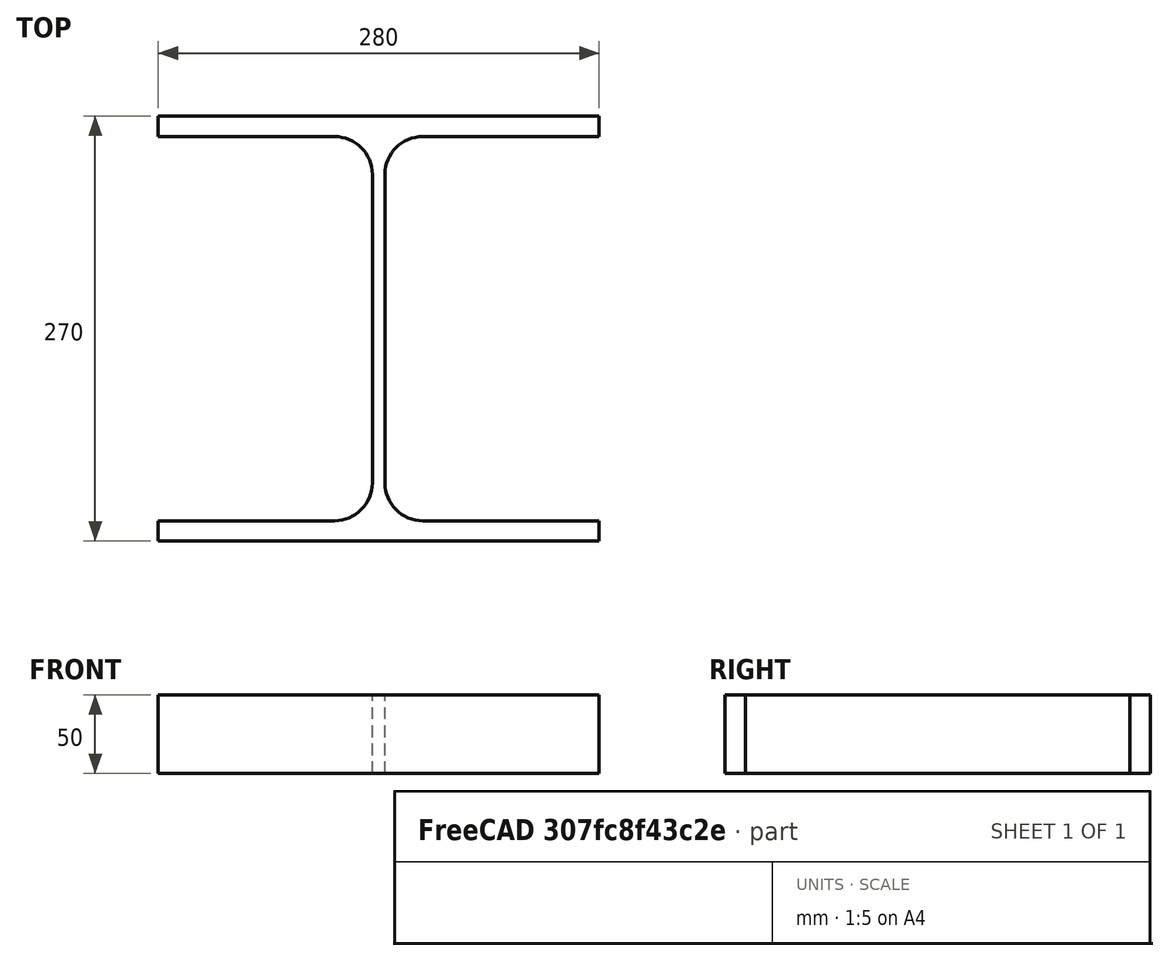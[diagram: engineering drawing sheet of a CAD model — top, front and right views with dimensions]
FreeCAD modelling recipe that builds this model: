
FCSTD DOCUMENT  (FreeCAD 0.15R4671 (Git))
Label: HE-A-Profile 280 DIN1025-3 S235JR
License: All rights reserved
LicenseURL: http://en.wikipedia.org/wiki/All_rights_reserved
objects: Sketcher::SketchObject×1, Part::Extrusion×1
note: 2 computed .brp shape members not serialized (recipe doc carries the construction recipe); baked Part::Feature solids carry a one-line shape summary decoded from their .brp

FEATURE [Sketcher::SketchObject] Sketch
  sketch-geometry (16):
    g0: LineSegment StartX=4 StartY=-98 StartZ=0 EndX=4 EndY=98 EndZ=0
    g1: LineSegment StartX=28 StartY=122 StartZ=0 EndX=140 EndY=122 EndZ=0
    g2: LineSegment StartX=140 StartY=122 StartZ=0 EndX=140 EndY=135 EndZ=0
    g3: LineSegment StartX=140 StartY=135 StartZ=0 EndX=-140 EndY=135 EndZ=0
    g4: LineSegment StartX=-140 StartY=135 StartZ=0 EndX=-140 EndY=122 EndZ=0
    g5: LineSegment StartX=-140 StartY=122 StartZ=0 EndX=-28 EndY=122 EndZ=0
    g6: LineSegment StartX=-4 StartY=98 StartZ=0 EndX=-4 EndY=-98 EndZ=0
    g7: LineSegment StartX=-28 StartY=-122 StartZ=0 EndX=-140 EndY=-122 EndZ=0
    g8: LineSegment StartX=-140 StartY=-122 StartZ=0 EndX=-140 EndY=-135 EndZ=0
    g9: LineSegment StartX=-140 StartY=-135 StartZ=0 EndX=140 EndY=-135 EndZ=0
    g10: LineSegment StartX=140 StartY=-135 StartZ=0 EndX=140 EndY=-122 EndZ=0
    g11: LineSegment StartX=140 StartY=-122 StartZ=0 EndX=28 EndY=-122 EndZ=0
    g12: ArcOfCircle CenterX=28 CenterY=98 CenterZ=0 NormalX=0 NormalY=0 NormalZ=1 Radius=24 StartAngle=1.5708 EndAngle=3.14159
    g13: ArcOfCircle CenterX=28 CenterY=-98 CenterZ=0 NormalX=0 NormalY=0 NormalZ=1 Radius=24 StartAngle=3.14159 EndAngle=4.71239
    g14: ArcOfCircle CenterX=-28 CenterY=98 CenterZ=0 NormalX=0 NormalY=0 NormalZ=1 Radius=24 StartAngle=0 EndAngle=1.5708
    g15: ArcOfCircle CenterX=-28 CenterY=-98 CenterZ=0 NormalX=0 NormalY=0 NormalZ=1 Radius=24 StartAngle=4.71239 EndAngle=6.28319
  constraints (42):
    c: Vertical(g0)
    c: Coincident(g2,g1)
    c: Vertical(g2)
    c: Coincident(g3,g2)
    c: Coincident(g4,g3)
    c: Vertical(g4)
    c: Coincident(g5,g4)
    c: Horizontal(g5)
    c: Vertical(g6)
    c: Horizontal(g7)
    c: Coincident(g8,g7)
    c: Vertical(g8)
    c: Coincident(g9,g8)
    c: Horizontal(g9)
    c: Coincident(g10,g9)
    c: Vertical(g10)
    c: Coincident(g11,g10)
    c: Horizontal(g11)
    c: Tangent(g1,g12) = 1.5708
    c: Tangent(g0,g12) = 1.5708
    c: Tangent(g0,g13) = 1.5708
    c: Tangent(g11,g13) = 1.5708
    c: Tangent(g5,g14) = 1.5708
    c: Tangent(g6,g14) = 1.5708
    c: Tangent(g6,g15) = 1.5708
    c: Tangent(g7,g15) = 1.5708
    c: Equal(g3,g9)
    c: Equal(g2,g4)
    c: Equal(g4,g8)
    c: Equal(g8,g10)
    c: Equal(g12,g14)
    c: Equal(g14,g15)
    c: Equal(g15,g13)
    c: Symmetric(g2,g3,g-2)
    c: Symmetric(g9,g8,g-2)
    c: Symmetric(g0,g6,g-2)
    c: Symmetric(g2,g9,g-1)
    c: DistanceY(g2,g9) = -270
    c: DistanceX(g3) = -280
    c: DistanceX(g0,g6) = -8
    c: DistanceY(g2) = 13
    c: Radius(g12) = 24
FEATURE [Part::Extrusion] Extrude  label="HE-A-Profile 280 DIN1025-3 S235JR"
  Base = -> Sketch
  Dir = (0,0,50)
  Solid = true
